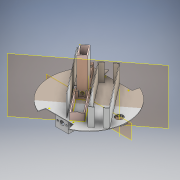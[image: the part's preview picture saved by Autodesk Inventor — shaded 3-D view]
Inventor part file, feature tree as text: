
AUTODESK INVENTOR PART (.ipt)
format: ipt  version: 2020 (Build 240168000, 168)  size: 506,880 bytes
history: native  units: mm
features: other x7, sketch x7, plane x2, extrude x1, mirror x1
ambient origin geometry x8: Origin, YZ Plane, XZ Plane, XY Plane, X Axis, Y Axis, Z Axis, Center Point
bodies: Solid1 (feature_tree)
feature tree (18):
  other  "Donja_konstrinkcija_s_drop_mehanizmom_v.2.0.iam"
  other  "KonstrukcijaDonjiDio_v.1.1.ipt:1"
  other  "DropMechanism_v.2.0.ipt:1"
  extrude  "Extrusion1"  Depth=8.0mm
  plane  "Work Plane2"
  mirror  "Mirror1"
  sketch  "Sketch2"  dims[d0=10.0mm d1=8.0mm]
  sketch  "Sketch30"
  sketch  "Sketch31"
  sketch  "Sketch37"
  plane  "Work Plane1"
  other  "Work Axis1"
  other  "Work Axis2"
  sketch  "Sketch3"  dims[d2=8.0mm]
  sketch  "Sketch4"  dims[d3=34.0mm d4=0.0mm]
  other  "Srf1"
  sketch  "Sketch8"
  other  "Srf1::Derived"
